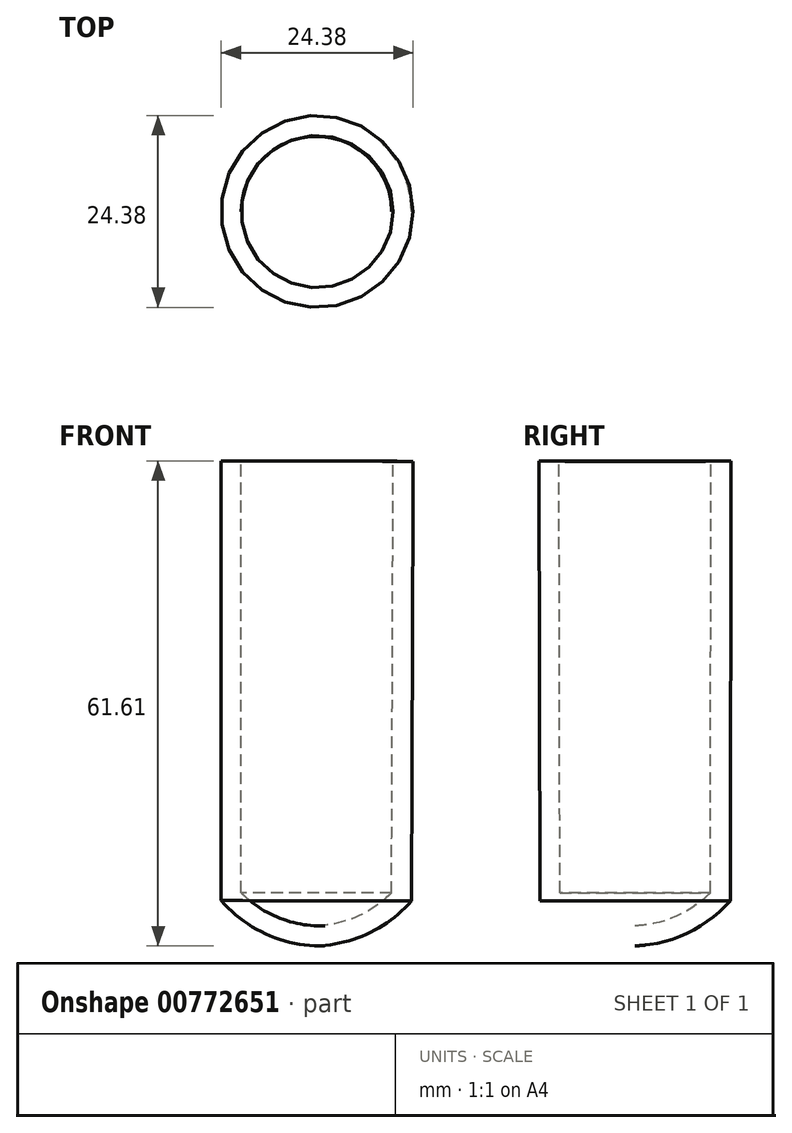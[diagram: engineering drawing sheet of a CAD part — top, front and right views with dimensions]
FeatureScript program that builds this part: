
annotation { "Feature Type Name" : "Feature", "Feature Type Description" : "" }
export const myFeature = defineFeature(function(context is Context, id is Id, definition is map)
    precondition{}
    {
        {
            var Q0;
            Q0=qCreatedBy(makeId("Front.planeOp"),FACE);
            var sketch = newSketch(context, id + "F0", { "sketchPlane" : qUnion([Q0])});
            skLineSegment(sketch, "E0", {"start": v(0, 45.04) * mm, "end": v(-12.2, 45.04) * mm});
            skLineSegment(sketch, "E1", {"start": v(-12.2, 45.04) * mm, "end": v(-12.2, -10.8) * mm});
            skArc(sketch, "E2", {"start": v(-12.2, -10.8) * mm, "mid": v(-6.75, -14.94) * mm, "end": v(-0.11, -16.56) * mm});
            skPoint(sketch, "E3", {"position": v(-0.11, -16.56) * mm});
            skLineSegment(sketch, "E4", {"start": v(0, 45.04) * mm, "end": v(-0.11, -16.56) * mm});
            skSolve(sketch);
        }
        {
            var Q0;
            Q0=makeQuery(id+"F0.imprint","IMPRINT",FACE,{"disambiguationData":[TD([[makeQuery(id+"F0.imprint","IMPRINT",EDGE,{"derivedFrom":sQuery(id+"F0.wireOp",EDGE,"E0")}),1.0]])]});
            var Q1;
            Q1=sQuery(id+"F0.wireOp",EDGE,"E4");
            revolve(context, id + "F1", {"entities" : qUnion([Q0]), "axis" : qUnion([Q1]), "revolveType" : RevolveType.FULL});
        }
        {
            var Q0;
            Q0=makeQuery(id+"F1.opRevolve","SWEPT_FACE",FACE,{"disambiguationData":[OSD([sQuery(id+"F0.wireOp",EDGE,"E0")])]});
            shell(context, id + "F2", {"entities" : qUnion([Q0]), "thickness" : 2.54 * mm});
        }
    });
